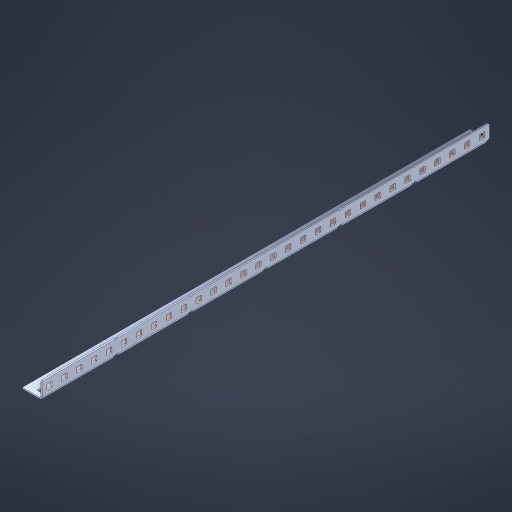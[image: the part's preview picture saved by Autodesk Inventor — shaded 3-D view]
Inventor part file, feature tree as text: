
AUTODESK INVENTOR PART (.ipt)
format: ipt  version: 2023 (Build 270158000, 158)  size: 960,512 bytes
history: native  units: in
note: dims shown in document units (in); Inventor stores cm internally (conversion verified against a paired STEP export)
features: other x65, extrude x59, sheet_metal_op x10, sketch x8, mirror x1, pattern_linear x1, chamfer x1
ambient origin geometry x8: Origin, YZ Plane, XZ Plane, XY Plane, X Axis, Y Axis, Z Axis, Center Point
bodies: Solid1 (feature_tree), Body (feature_tree)
feature tree (145):
  other  "Flange Pattern Plane"
  sheet_metal_op  "Flange Pattern"
  sheet_metal_op  "Body Pattern"
  other  "Arc Length"
  mirror  "Notch Mirror"
  pattern_linear  "Notch Pattern"  Spacing1=0.1875in  [1 undecoded]
  chamfer  "End Chamfer"
  extrude  "Half Cut"  Depth=0.0469in
  sketch  "Sketch1"  dims[d0=2.5in]
  other  "Plate1"
  sketch  "Sketch2"  dims[d1=15.0in]
  other  "Plate2"
  sheet_metal_op  "Bend1"
  sheet_metal_op  "Corner1"
  sketch  "Sketch3"  dims[d2=0.0469in]
  other  "Flange Pattern Sketch"
  sketch  "Sketch7"  dims[d3=0.0469in]
  other  "Srf1"
  other  "Srf2"
  sketch  "Sketch8"  dims[d4=0.0234in]
  sketch  "Sketch9"  dims[d5=0.0938in]
  other  "Srf91"
  sheet_metal_op  "Body Pattern Sketch"
  other  "Srf92"
  sketch  "Sketch13"  dims[d6=0.0469in]
  sketch  "Sketch14"  dims[d7=0.5in d8=90.0deg d9=0.0312in d10=0.1875in d11=0.0469in d12=0.0469in d16=0.182in d17=0.02in d18=0.0469in d19=0.0in d20=0.25in d21=0.25in d46=0.172in d47=1.0in d48=0.0in d49=0.182in d50=0.02in d51=0.25in d52=0.25in d53=0.0469in d54=0.0in d55=0.172in d56=1.0in d57=0.0in d60=11.811in d62=0.5in d63=0.3937in d65=0.5in d85=0.1227in d86=0.1659in d88=0.04in d89=0.0469in d90=0.0in d91=0.04in d92=0.0491in d95=2.5in d96=0.04in d97=0.25in d98=45.0deg d101=0.0in d102=2.497in d131=0.5in d132=11.811in d134=0.5in d139=0.5in]
  other  "Srf856"
  other  "Srf1310"
  other  "Srf1311"
  other  "Srf1312"
  other  "Srf1376"
  other  "Srf1377"
  other  "Srf1728"
  other  "Srf1755"
  other  "Srf1878"
  other  "Srf1879"
  other  "Srf1880"
  other  "Srf1881"
  other  "Srf1882"
  other  "Srf1883"
  other  "Srf1884"
  other  "Srf1885"
  other  "Srf1886"
  other  "Srf1887"
  other  "Srf1888"
  other  "Srf1889"
  other  "Srf1890"
  other  "Srf1891"
  other  "Srf1892"
  other  "Srf1893"
  other  "Srf1894"
  other  "Srf1895"
  other  "Srf1896"
  other  "Srf1897"
  other  "Srf1898"
  other  "Srf1899"
  other  "Srf1900"
  other  "Srf1901"
  other  "Srf1942"
  other  "Srf1943"
  other  "Srf1944"
  other  "Srf1945"
  other  "Srf1946"
  other  "Srf1947"
  other  "Srf1948"
  other  "Srf1949"
  other  "Srf1950"
  other  "Srf1951"
  other  "Srf1952"
  other  "Srf1953"
  other  "Srf1954"
  other  "Srf1955"
  other  "Srf1956"
  other  "Srf1957"
  other  "Srf1958"
  other  "Srf1959"
  other  "Srf1960"
  other  "Srf1961"
  other  "Srf1962"
  other  "Srf1963"
  other  "Srf1964"
  other  "Srf1965"
  sheet_metal_op  "Flange Stamp"
  sheet_metal_op  "Flange Circle"
  sheet_metal_op  "Body Stamp"
  sheet_metal_op  "Body Circle"
  sheet_metal_op  "Notch"
  extrude  "ExtrusionSrf2"  Depth=0.0469in
  extrude  "ExtrusionSrf92"  Depth=0.0469in
  extrude  "ExtrusionSrf856"  Depth=0.02in
  extrude  "ExtrusionSrf1310"  Depth=0.0469in
  extrude  "ExtrusionSrf1311"  TaperAngle=0.0deg  [1 undecoded]
  extrude  "ExtrusionSrf1312"  Depth=0.0469in
  extrude  "ExtrusionSrf1376"  Depth=0.0469in
  extrude  "ExtrusionSrf1377"  Depth=0.0469in
  extrude  "ExtrusionSrf1728"  Depth=0.0469in TaperAngle=0.0deg
  extrude  "ExtrusionSrf1755"  Depth=0.0469in
  extrude  "ExtrusionSrf1878"  Depth=0.02in
  extrude  "ExtrusionSrf1879"  Depth=0.0469in
  extrude  "ExtrusionSrf1880"  Depth=0.0469in
  extrude  "ExtrusionSrf1881"  Depth=0.0469in
  extrude  "ExtrusionSrf1882"  TaperAngle=0.0deg  [1 undecoded]
  extrude  "ExtrusionSrf1883"  Depth=0.0469in
  extrude  "ExtrusionSrf1884"  Depth=0.0469in TaperAngle=0.0deg
  extrude  "ExtrusionSrf1885"  Depth=0.0469in
  extrude  "ExtrusionSrf1886"  Depth=0.3937in
  extrude  "ExtrusionSrf1887"  Depth=0.0469in
  extrude  "ExtrusionSrf1888"  Depth=0.0469in
  extrude  "ExtrusionSrf1889"  Depth=0.0469in
  extrude  "ExtrusionSrf1890"  Depth=0.0469in
  extrude  "ExtrusionSrf1891"  TaperAngle=0.0deg  [1 undecoded]
  extrude  "ExtrusionSrf1892"  Depth=0.0469in
  extrude  "ExtrusionSrf1893"  Depth=0.0469in
  extrude  "ExtrusionSrf1894"  Depth=0.0469in
  extrude  "ExtrusionSrf1895"  Depth=0.0469in TaperAngle=45.0deg
  extrude  "ExtrusionSrf1896"  TaperAngle=0.0deg  [1 undecoded]
  extrude  "ExtrusionSrf1897"  Depth=0.0469in
  extrude  "ExtrusionSrf1898"  Depth=0.0469in
  extrude  "ExtrusionSrf1899"  Depth=0.0469in
  extrude  "ExtrusionSrf1900"  Depth=0.0469in
  extrude  "ExtrusionSrf1901"  Depth=0.0469in
  extrude  "ExtrusionSrf1942"  [1 undecoded]
  extrude  "ExtrusionSrf1943"  [1 undecoded]
  extrude  "ExtrusionSrf1944"  [1 undecoded]
  extrude  "ExtrusionSrf1945"  [1 undecoded]
  extrude  "ExtrusionSrf1946"  [1 undecoded]
  extrude  "ExtrusionSrf1947"  [1 undecoded]
  extrude  "ExtrusionSrf1948"  [1 undecoded]
  extrude  "ExtrusionSrf1949"  [1 undecoded]
  extrude  "ExtrusionSrf1950"  [1 undecoded]
  extrude  "ExtrusionSrf1951"  [1 undecoded]
  extrude  "ExtrusionSrf1952"  [1 undecoded]
  extrude  "ExtrusionSrf1953"  [1 undecoded]
  extrude  "ExtrusionSrf1954"  [1 undecoded]
  extrude  "ExtrusionSrf1955"  [1 undecoded]
  extrude  "ExtrusionSrf1956"  [1 undecoded]
  extrude  "ExtrusionSrf1957"  [1 undecoded]
  extrude  "ExtrusionSrf1958"  [1 undecoded]
  extrude  "ExtrusionSrf1959"  [1 undecoded]
  extrude  "ExtrusionSrf1960"  [1 undecoded]
  extrude  "ExtrusionSrf1961"  [1 undecoded]
  extrude  "ExtrusionSrf1962"  [1 undecoded]
  extrude  "ExtrusionSrf1963"  [1 undecoded]
  extrude  "ExtrusionSrf1964"  [1 undecoded]
  extrude  "ExtrusionSrf1965"  [1 undecoded]
note: 29 required parameter values undecoded (feature->parameter linkage not recoverable at this tier; creation-order binding heuristic only, values carry confidence <= 0.55)
